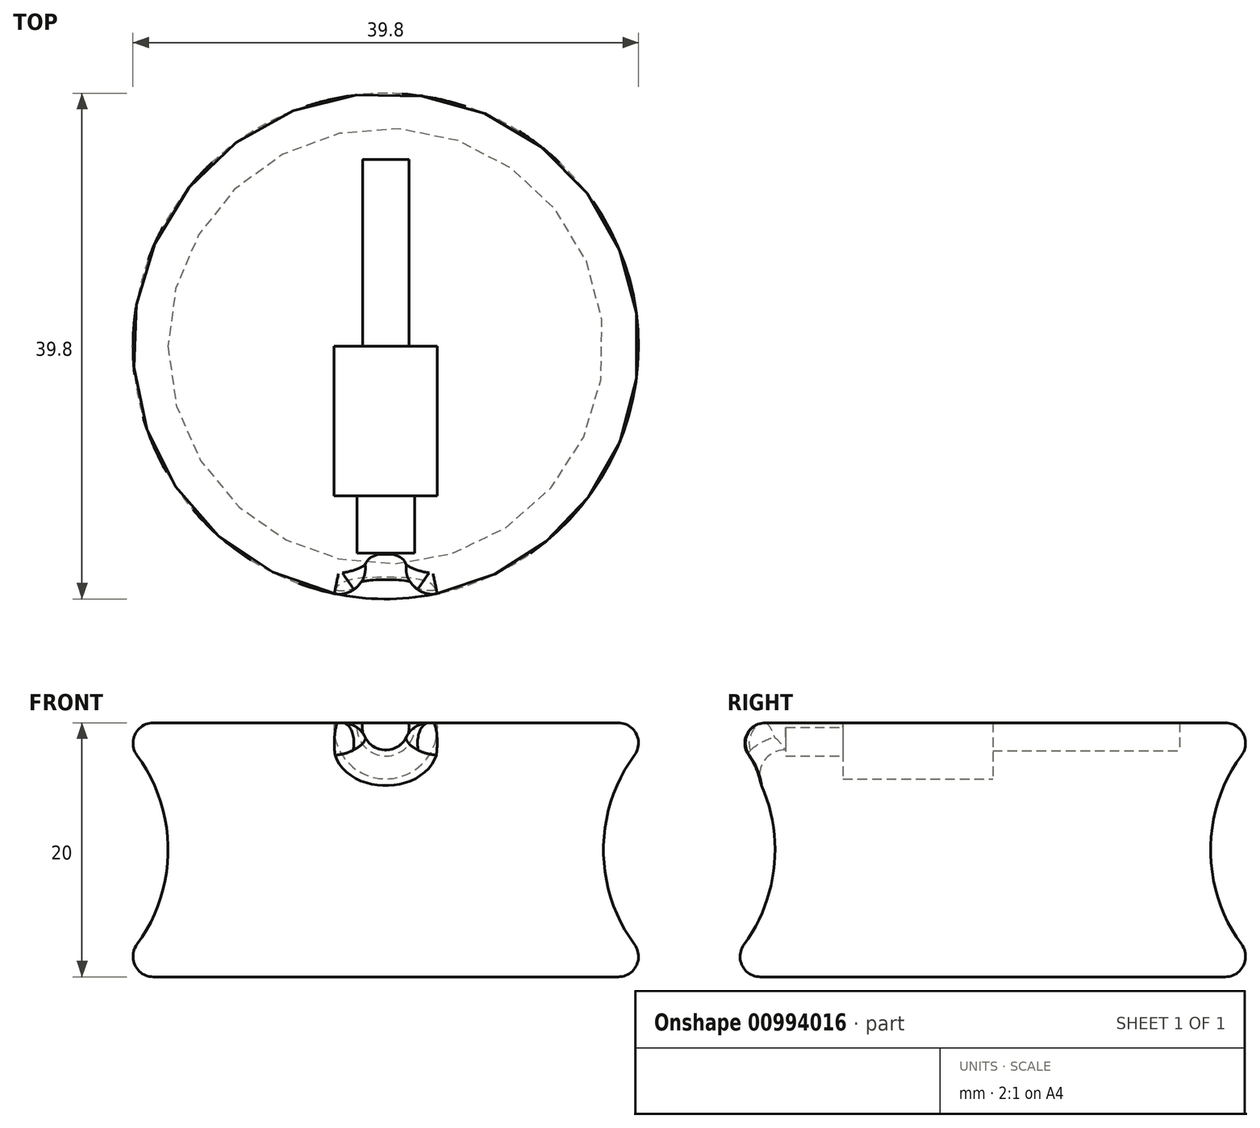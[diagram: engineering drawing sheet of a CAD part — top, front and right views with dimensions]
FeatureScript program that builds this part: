
annotation { "Feature Type Name" : "Feature", "Feature Type Description" : "" }
export const myFeature = defineFeature(function(context is Context, id is Id, definition is map)
    precondition{}
    {
        {
            var Q0;
            Q0=qCreatedBy(makeId("Front.planeOp"),FACE);
            var sketch = newSketch(context, id + "F0", { "sketchPlane" : qUnion([Q0])});
            skLineSegment(sketch, "E0", {"start": v(0, 0) * mm, "end": v(0, 10) * mm});
            skLineSegment(sketch, "E1", {"start": v(0, 10) * mm, "end": v(18.3, 10) * mm});
            skLineSegment(sketch, "E2.MirrorCS", {"start": v(0, 0) * mm, "end": v(0, -10) * mm});
            skLineSegment(sketch, "E3.MirrorCS", {"start": v(0, -10) * mm, "end": v(18.3, -10) * mm});
            skArc(sketch, "E4", {"start": v(19.59, 7.45) * mm, "mid": v(17.15, 0) * mm, "end": v(19.59, -7.45) * mm});
            skArc(sketch, "E5.filletArc", {"start": v(19.59, 7.45) * mm, "mid": v(19.73, 9.12) * mm, "end": v(18.3, 10) * mm});
            skPoint(sketch, "E6.visualSharp", {"position": v(22.1, -10) * mm});
            skArc(sketch, "E6.filletArc", {"start": v(18.3, -10) * mm, "mid": v(19.73, -9.12) * mm, "end": v(19.59, -7.45) * mm});
            skPoint(sketch, "E7.third.point", {"position": v(19.59, 7.45) * mm});
            skSolve(sketch);
        }
        {
            var Q0;
            Q0 = qSketchRegion(id + "F0", true);
            var Q1;
            Q1=sQuery(id+"F0.wireOp",EDGE,"E0");
            revolve(context, id + "F1", {"surfaceOperationType" : NewSurfaceOperationType.NEW, "entities" : qUnion([Q0]), "axis" : qUnion([Q1]), "revolveType" : RevolveType.FULL});
        }
        {
            var Q0;
            Q0=makeQuery(id+"F1.opRevolve","SWEPT_FACE",FACE,{"disambiguationData":[OSD([sQuery(id+"F0.wireOp",EDGE,"E1")])]});
            var sketch = newSketch(context, id + "F2", { "sketchPlane" : qUnion([Q0])});
            skLineSegment(sketch, "E8", {"start": v(0, 0) * mm, "end": v(0, 7.76) * mm, "construction": true});
            skLineSegment(sketch, "E9", {"start": v(0, 14.7) * mm, "end": v(1.85, 14.7) * mm});
            skLineSegment(sketch, "E10", {"start": v(1.85, 14.7) * mm, "end": v(1.85, 0) * mm});
            skLineSegment(sketch, "E11", {"start": v(1.85, 0) * mm, "end": v(4.08, 0) * mm});
            skLineSegment(sketch, "E12", {"start": v(4.08, 0) * mm, "end": v(4.08, -11.8) * mm});
            skLineSegment(sketch, "E13", {"start": v(4.08, -11.8) * mm, "end": v(2.27, -11.8) * mm});
            skLineSegment(sketch, "E14", {"start": v(2.28, -11.8) * mm, "end": v(2.28, -16.3) * mm});
            skLineSegment(sketch, "E15", {"start": v(0, -32.12) * mm, "end": v(0, 14.7) * mm});
            skLineSegment(sketch, "E16", {"start": v(2.28, -16.3) * mm, "end": v(1.8, -16.3) * mm});
            skLineSegment(sketch, "E17", {"start": v(1.8, -16.3) * mm, "end": v(1.8, -32.12) * mm});
            skLineSegment(sketch, "E18", {"start": v(1.8, -32.12) * mm, "end": v(0, -32.12) * mm});
            skSolve(sketch);
        }
        {
            var Q0;
            Q0 = qSketchRegion(id + "F2", true);
            var Q1;
            Q1=sQuery(id+"F2.wireOp",EDGE,"E15");
            revolve(context, id + "F3", {"surfaceOperationType" : NewSurfaceOperationType.NEW, "entities" : qUnion([Q0]), "axis" : qUnion([Q1]), "revolveType" : RevolveType.FULL, "oppositeDirection" : true});
        }
        {
            var Q0;
            Q0=makeQuery(id+"F3.opRevolve","SWEPT_BODY",BODY,{"disambiguationData":[OSD([sQuery(id+"F2.wireOp",EDGE,"E9"),sQuery(id+"F2.wireOp",EDGE,"E10"),sQuery(id+"F2.wireOp",EDGE,"E11"),sQuery(id+"F2.wireOp",EDGE,"E12"),sQuery(id+"F2.wireOp",EDGE,"E13"),sQuery(id+"F2.wireOp",EDGE,"E14"),sQuery(id+"F2.wireOp",EDGE,"tOqfYI2w-CfAX-tWnE-h2EW-kLbGOTdadPNf"),sQuery(id+"F2.wireOp",EDGE,"ORCtReXa-SAzl-0I2L-zCPc-lYK8wpV2loMg"),sQuery(id+"F2.wireOp",EDGE,"E15")])]});
            transform(context, id + "F4", {"entities" : qUnion([Q0]), "transformType" : TransformType.TRANSLATION_3D, "dx" : 0 * mm, "dy" : 0 * mm, "dz" : -0.34 * mm, "makeCopy" : false});
        }
        {
            var Q0;
            Q0=makeQuery(id+"F3.opRevolve","SWEPT_BODY",BODY,{"disambiguationData":[OSD([sQuery(id+"F2.wireOp",EDGE,"E9"),sQuery(id+"F2.wireOp",EDGE,"E10"),sQuery(id+"F2.wireOp",EDGE,"E11"),sQuery(id+"F2.wireOp",EDGE,"E12"),sQuery(id+"F2.wireOp",EDGE,"E13"),sQuery(id+"F2.wireOp",EDGE,"E14"),sQuery(id+"F2.wireOp",EDGE,"tOqfYI2w-CfAX-tWnE-h2EW-kLbGOTdadPNf"),sQuery(id+"F2.wireOp",EDGE,"ORCtReXa-SAzl-0I2L-zCPc-lYK8wpV2loMg"),sQuery(id+"F2.wireOp",EDGE,"E15")])]});
            var Q1;
            Q1=makeQuery(id+"F1.opRevolve","SWEPT_BODY",BODY,{"disambiguationData":[OSD([sQuery(id+"F0.wireOp",EDGE,"E0"),sQuery(id+"F0.wireOp",EDGE,"E1"),sQuery(id+"F0.wireOp",EDGE,"E2.MirrorCS"),sQuery(id+"F0.wireOp",EDGE,"E3.MirrorCS"),sQuery(id+"F0.wireOp",EDGE,"E4"),sQuery(id+"F0.wireOp",EDGE,"E5.filletArc"),sQuery(id+"F0.wireOp",EDGE,"E6.filletArc")])]});
            booleanBodies(context, id + "F5", {"operationType" : BooleanOperationType.SUBTRACTION, "tools" : qUnion([Q0]), "targets" : qUnion([Q1])});
        }
        {
            var Q0;
            Q0=makeQuery(id+"F5.opBoolean","INTERSECT",EDGE,{"derivedFrom":[makeQuery(id+"F1.opRevolve","SWEPT_FACE",FACE,{"disambiguationData":[OSD([sQuery(id+"F0.wireOp",EDGE,"E5.filletArc")])]}),makeQuery(id+"F3.opRevolve","SWEPT_FACE",FACE,{"disambiguationData":[OSD([sQuery(id+"F2.wireOp",EDGE,"E17")])]})]});
            fillet(context, id + "F6", {"entities" : qUnion([Q0]), "radius" : 2 * mm, "tangentPropagation" : true, "allowEdgeOverflow" : false});
        }
    });
